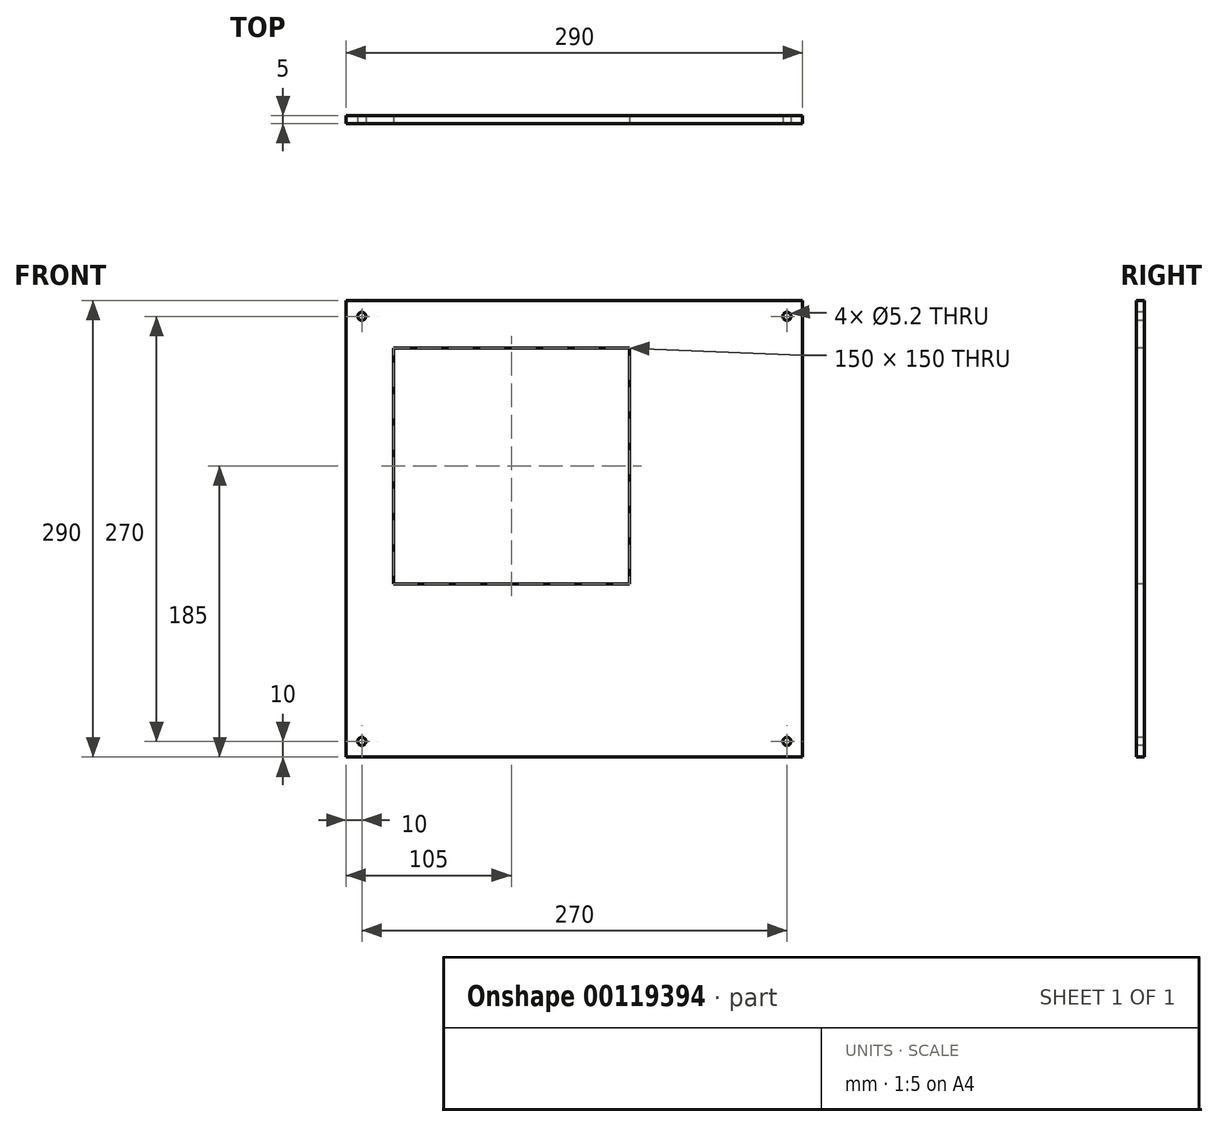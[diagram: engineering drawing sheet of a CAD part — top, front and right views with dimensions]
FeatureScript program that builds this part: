
annotation { "Feature Type Name" : "Feature", "Feature Type Description" : "" }
export const myFeature = defineFeature(function(context is Context, id is Id, definition is map)
    precondition{}
    {
        {
            var Q0;
            Q0=qCreatedBy(makeId("Front.planeOp"),FACE);
            var sketch = newSketch(context, id + "F0", { "sketchPlane" : qUnion([Q0])});
            skLineSegment(sketch, "E0.bottom", {"start": v(145, -145) * mm, "end": v(-145, -145) * mm});
            skLineSegment(sketch, "E0.top", {"start": v(145, 145) * mm, "end": v(-145, 145) * mm});
            skLineSegment(sketch, "E0.left", {"start": v(145, -145) * mm, "end": v(145, 145) * mm});
            skLineSegment(sketch, "E0.right", {"start": v(-145, -145) * mm, "end": v(-145, 145) * mm});
            skPoint(sketch, "E0.middle", {"position": v(0, 0) * mm});
            skSolve(sketch);
        }
        {
            var Q0;
            Q0=makeQuery(id+"F0.imprint","IMPRINT",FACE,{"disambiguationData":[TD([[makeQuery(id+"F0.imprint","IMPRINT",EDGE,{"derivedFrom":sQuery(id+"F0.wireOp",EDGE,"E0.bottom")}),-1.0]])]});
            extrude(context, id + "F1", {"entities" : qUnion([Q0]), "depth" : 5 * mm});
        }
        {
            var Q0;
            Q0=makeQuery(id+"F1.opExtrude","CAP_FACE",FACE,{"disambiguationData":[OSD([sQuery(id+"F0.wireOp",EDGE,"E0.bottom"),sQuery(id+"F0.wireOp",EDGE,"E0.top"),sQuery(id+"F0.wireOp",EDGE,"E0.left"),sQuery(id+"F0.wireOp",EDGE,"E0.right")])],"isStart":false});
            var sketch = newSketch(context, id + "F2", { "sketchPlane" : qUnion([Q0])});
            skCircle(sketch, "E1", {"center": v(-135, 135) * mm, "radius": 2.6 * mm});
            skCircle(sketch, "E2.0.1.0", {"center": v(-135, -135) * mm, "radius": 2.6 * mm});
            skCircle(sketch, "E2.1.0.0", {"center": v(135, 135) * mm, "radius": 2.6 * mm});
            skCircle(sketch, "E2.1.1.0", {"center": v(135, -135) * mm, "radius": 2.6 * mm});
            skCircle(sketch, "E2.2.0.0", {"center": v(405, 135) * mm, "radius": 2.6 * mm});
            skCircle(sketch, "E2.2.1.0", {"center": v(405, -135) * mm, "radius": 2.6 * mm});
            skLineSegment(sketch, "E2.direction1", {"start": v(-135, 135) * mm, "end": v(135, 135) * mm, "construction": true});
            skLineSegment(sketch, "E2.direction2", {"start": v(-135, 135) * mm, "end": v(-135, -135) * mm, "construction": true});
            skSolve(sketch);
        }
        {
            var Q0;
            Q0 = qSketchRegion(id + "F2", true);
            extrude(context, id + "F3", {"entities" : qUnion([Q0]), "operationType" : NewBodyOperationType.REMOVE, "endBound" : BoundingType.THROUGH_ALL, "oppositeDirection" : true, "depth" : 25 * mm});
        }
        {
            var Q0;
            Q0=makeQuery(id+"F1.opExtrude","CAP_FACE",FACE,{"disambiguationData":[OSD([sQuery(id+"F0.wireOp",EDGE,"E0.bottom"),sQuery(id+"F0.wireOp",EDGE,"E0.top"),sQuery(id+"F0.wireOp",EDGE,"E0.left"),sQuery(id+"F0.wireOp",EDGE,"E0.right")])],"isStart":false});
            var sketch = newSketch(context, id + "F4", { "sketchPlane" : qUnion([Q0])});
            skLineSegment(sketch, "E3.bottom", {"start": v(-115, 115) * mm, "end": v(35, 115) * mm});
            skLineSegment(sketch, "E3.top", {"start": v(-115, -35) * mm, "end": v(35, -35) * mm});
            skLineSegment(sketch, "E3.left", {"start": v(-115, 115) * mm, "end": v(-115, -35) * mm});
            skLineSegment(sketch, "E3.right", {"start": v(35, 115) * mm, "end": v(35, -35) * mm});
            skSolve(sketch);
        }
        {
            var Q0;
            Q0=makeQuery(id+"F4.imprint","IMPRINT",FACE,{"disambiguationData":[TD([[makeQuery(id+"F4.imprint","IMPRINT",EDGE,{"derivedFrom":sQuery(id+"F4.wireOp",EDGE,"E3.bottom")}),-1.0]])]});
            extrude(context, id + "F5", {"entities" : qUnion([Q0]), "operationType" : NewBodyOperationType.REMOVE, "endBound" : BoundingType.THROUGH_ALL, "oppositeDirection" : true, "depth" : 25 * mm});
        }
    });
